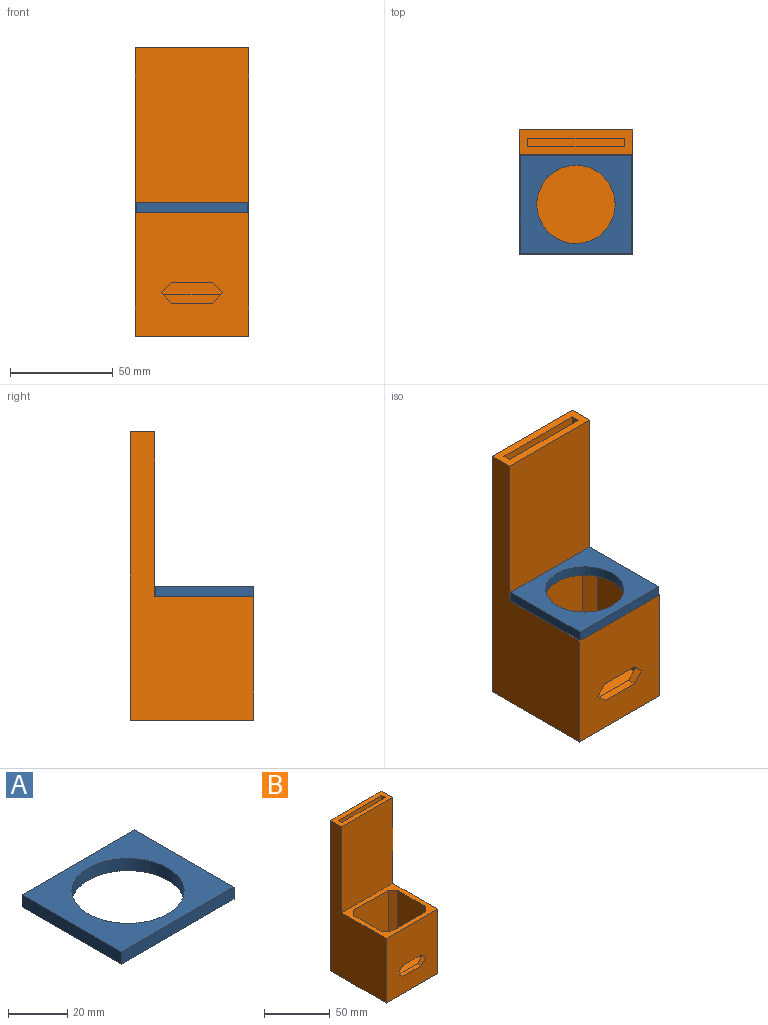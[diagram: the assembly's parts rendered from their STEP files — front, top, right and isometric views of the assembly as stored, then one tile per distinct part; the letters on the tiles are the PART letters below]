
ASSEMBLY  parts=2 mates=1
PART A: 7 faces, bbox 54x47.5x5 mm
  f0: plane 47.5x5mm, normal (1,0,0), area 237.5mm2, adj f1,f4,f5,f6
  f1: plane 54x5mm, normal (0,1,0), area 270mm2, adj f0,f2,f5,f6
  f2: plane 47.5x5mm, normal (-1,0,0), area 237.5mm2, adj f1,f4,f5,f6
  f3: cylinder r=19mm len=38mm, axis (0,0,-1), area 596.9mm2, adj f5,f6
  f4: plane 54x5mm, normal (0,-1,0), area 270mm2, adj f0,f2,f5,f6
  f5: plane 54x47.5mm, normal (0,0,1), area 1430.9mm2, adj f0,f1,f2,f3,f4
  f6: plane 54x47.5mm, normal (0,0,-1), area 1430.9mm2, adj f0,f1,f2,f3,f4
PART B: 32 faces, bbox 55x60x140 mm
  f0: plane 55x47.97mm, normal (0,0,1), area 809.8mm2, adj f1,f2,f3,f4,f6,f8,f12,f13
  f1: plane 130x46.97mm, normal (1,0,0), area 2083.6mm2, adj f0,f7,f9,f10,f14,f16,f18,f22
  f2: plane 140x60mm, normal (-1,0,0), area 4562.3mm2, adj f0,f3,f5,f13,f14,f27
  f3: plane 60x55mm, normal (0,-1,0), area 3050mm2, adj f0,f2,f4,f19,f20,f23,f24,f25
  f4: plane 140x60mm, normal (1,0,0), area 4562.3mm2, adj f0,f3,f5,f13,f14,f27
  f5: plane 140x55mm, normal (0,1,0), area 7700mm2, adj f2,f4,f14,f27
  f6: plane 50x37mm, normal (0,1,0), area 1600mm2, adj f0,f10,f15,f16,f19,f20,f23,f24
  f7: plane 130x47mm, normal (0,-1,0), area 6110mm2, adj f1,f8,f10,f14
  f8: plane 130x46.97mm, normal (-1,0,0), area 2083.6mm2, adj f0,f7,f9,f10,f14,f15,f17,f21
  f9: plane 125x47mm, normal (0,1,0), area 5665mm2, adj f1,f8,f11,f14,f21,f22
  f10: plane 51.97x47mm, normal (0,0,1), area 2417.7mm2, adj f1,f6,f7,f8,f15,f16
  f11: plane 37x8mm, normal (0,0,-1), area 296mm2, adj f9,f12,f21,f22
  f12: plane 40x37mm, normal (0,-1,0), area 1480mm2, adj f0,f11,f17,f18
  f13: plane 80x55mm, normal (0,-1,0), area 4400mm2, adj f0,f2,f4,f14
  f14: plane 55x12.03mm, normal (0,0,1), area 473.5mm2, adj f1,f2,f4,f5,f7,f8,f9,f13
  f15: plane 50x5mm, normal (-0.71,0.71,0), area 353.6mm2, adj f0,f6,f8,f10
  f16: plane 50x5mm, normal (0.71,0.71,0), area 353.6mm2, adj f0,f1,f6,f10
  f17: plane 45x5mm, normal (-0.71,-0.71,0), area 300.5mm2, adj f0,f8,f12,f21
  f18: plane 45x5mm, normal (0.71,-0.71,0), area 300.5mm2, adj f0,f1,f12,f22
  f19: plane 20x4mm, normal (0,0,1), area 80mm2, adj f3,f6,f24,f26
  f20: plane 20x4mm, normal (0,0,-1), area 80mm2, adj f3,f6,f23,f25
  f21: plane 13x5mm, normal (-0.71,0,-0.71), area 74.2mm2, adj f8,f9,f11,f17
  f22: plane 13x5mm, normal (0.71,0,-0.71), area 74.2mm2, adj f1,f9,f11,f18
  f23: plane 5x5mm, normal (-0.71,0,-0.71), area 28.3mm2, adj f3,f6,f20,f24
  f24: plane 5x5mm, normal (-0.71,0,0.71), area 28.3mm2, adj f3,f6,f19,f23
  f25: plane 5x5mm, normal (0.71,0,-0.71), area 28.3mm2, adj f3,f6,f20,f26
  f26: plane 5x5mm, normal (0.71,0,0.71), area 28.3mm2, adj f3,f6,f19,f25
  f27: plane 60x55mm, normal (0,0,-1), area 2897.9mm2, adj f2,f3,f4,f5,f29,f31
  f28: plane 16x16mm, normal (0,0,-1), area 201.1mm2, adj f29
  f29: cylinder r=8mm len=16mm, axis (0,0,-1), area 226.2mm2, adj f27,f28
  f30: plane 16x16mm, normal (0,0,-1), area 201.1mm2, adj f31
  f31: cylinder r=8mm len=16mm, axis (0,0,-1), area 226.2mm2, adj f27,f30
PLACE A t=(21.62,-5.47,92.77)mm
PLACE B t=(-67.36,-5.71,38.77)mm
MATE fastened A.f3 <-> B.f0  axis (0,0,-1) through (-39.86,18.28,92.77)mm
